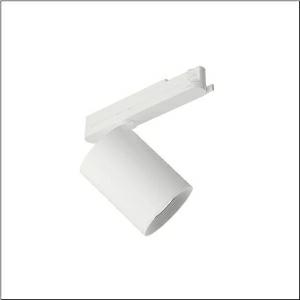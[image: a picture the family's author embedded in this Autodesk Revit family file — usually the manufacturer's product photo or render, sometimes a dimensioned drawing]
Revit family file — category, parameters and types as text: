
# Revit family: spot_21_51se12mbb5b
name_source: partatom
category: Lighting Fixtures
units: mm (PartAtom-declared; Revit-internal decimal feet)

## family parameters
Cut with Voids When Loaded = No
Host = Face
Light Source = No
Part Type = Normal
Room Calculation Point = No
Round Connector Dimension = Use Diameter
Shared = No

## types (1)
- --- (1 x LED, 5300 lm, 41.7 W, 3000K)
    Apparent Load = 42 VA
    CIE Flux Codes = 95 98 99 100 100
    Color Rendering = 90
    Color Temperature = 3000K
    Default Elevation = 1800 mm
    Description = Spot 21, directional spotlight, light control with lens, of PMMA, LED rated luminous flux: 5.100lm, light colour: 930, control gear: ECG Multilumen, with 3-phase adapter, mains connection: 220..240V, AC, 50/60Hz, of aluminium, traffic white (RAL 9016), length: 213mm, diameter: 105mm, protection rating (complete): IP20, insulation class (complete): insulation class I (protective earthing), certification: CE, impact resistance: IK02, permissible ambient temperature for indoor applications: -20..+40°C, packaging unit: 1 piece
    Height = 175 mm
    Lamp = 1 x LED
    Lamp Light Flux = 5300 lm
    Lamp Power = 41.7 W
    Lamp count = 1
    Length = 105 mm
    Luminous efficacy = 127 lm/W
    Manufacturer = Siteco
    ModVariant = No
    Model = 51SE12MBB5B
    Mounting Place = Ceiling
    Mounting Type = Pendant
    Number of Poles = 1
    OnlyDefault = Yes
    Power Factor = 1
    Product Name = Spot 21
    Product group = directional spotlight
    ProductGroupID = 904
    Protection Class = Protection class I
    Protection Degree = IP 20
    RLX_Detail_Level = 1
    RlxData = <blob elided: 17633 chars, md5=4e31b87c>
    Socket = socket
    Standby Power = 0 W
    System Light Flux = 5300 lm
    System Power = 42 W
    Type Comments = factory setting: luminous flux: 100 % | (ON | ON | ON | ON) | 1050 mA
    Type Image = l_1003976.jpg
    URL = http://relux.com
    VarID = @adj_053501
    Voltage = 0 V
    Weight = 0.00 kg
    Width = 0 mm  [stored 0 ft]

note: [stored X ft] marks values corroborated as IEEE doubles in the binary element streams (Revit-internal decimal feet)

## geometry (parser evidence)
native form markers: Blend x4, Sweep x10
no freeform markers — native parametric forms only
